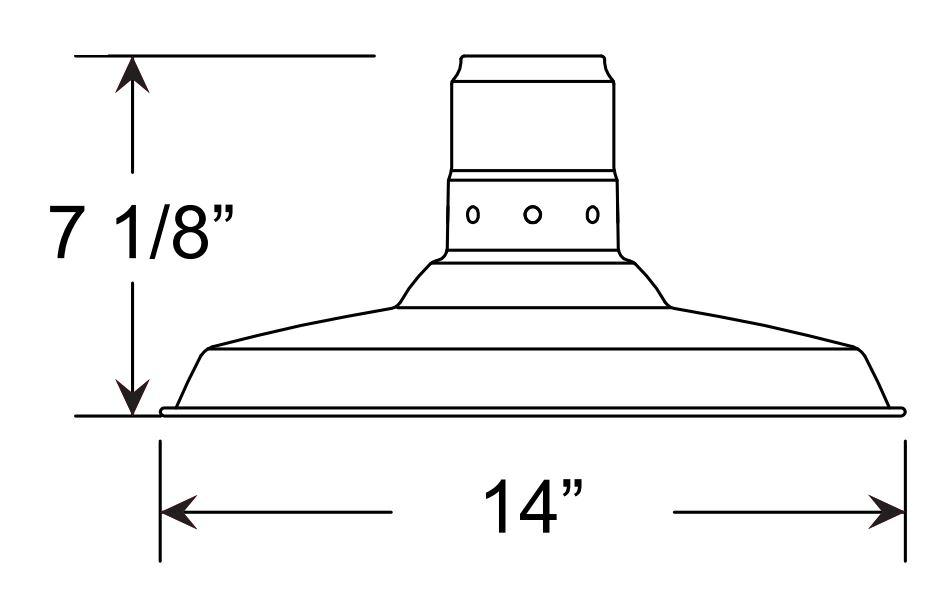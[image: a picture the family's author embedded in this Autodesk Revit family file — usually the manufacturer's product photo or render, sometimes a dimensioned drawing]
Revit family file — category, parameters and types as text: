
# Revit family: SPO-KEY-ORB MB
name_source: partatom
category: Lighting Fixtures
units: mm (PartAtom-declared; Revit-internal decimal feet)

## family parameters
Always vertical = Yes
Cut with Voids When Loaded = No
Light Source = Yes
OmniClass Number = 23.80.70.00
OmniClass Title = Lighting
Part Type = Normal
Room Calculation Point = No
Round Connector Dimension = Use Diameter
Shared = No
Work Plane-Based = No

## types (1)
- SPO-KEY-ORB
    Apparent Load = 60 VA
    Body Colour = Spun aluminium
    Body Material = body
    Color Filter = 16777215
    Construction Material = Heavy Duty spun aluminum.
    Default Elevation = 0' - 0"
    Description = 120-277 Voltage
    Dimming Lamp Color Temperature Shift = <None>
    Fixture Diameter = 0' - 1 1/2"
    Fixture Height = 0' - 3 1/2"
    GLASS = Glass
    Lamp = MED-BASE
    Load Classification = Lighting
    Manufacturer = ANP Lighting
    Model = SPO-KEY-ORB
    Photometric Web File = generic.ies
    Power Factor = 1
    Ring = RING
    SPO-KEY-ORB = Yes
    Tilt Angle = 90.00°
    URL = https://www.anplighting.com
    Voltage = 277 V
    Warranty = 5 year limited warranty
    Wattage Comments = 60W Max
    Weight = 0.30 lbs

## geometry (parser evidence)
native form markers: Sweep x21
no freeform markers — native parametric forms only
